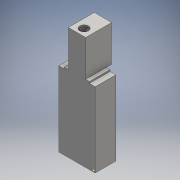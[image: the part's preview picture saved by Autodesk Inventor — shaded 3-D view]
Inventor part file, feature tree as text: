
AUTODESK INVENTOR PART (.ipt)
format: ipt  version: 2016 SP1 (Build 200210100, 210)  size: 351,744 bytes
history: native  units: mm
features: sketch x20, extrude x18, other x1
ambient origin geometry x8: Origin, YZ Plane, XZ Plane, XY Plane, X Axis, Y Axis, Z Axis, Center Point
bodies: Body1 (feature_tree)
feature tree (39):
  other  "Bryła1"
  extrude  "Wyciągnięcie proste1"  Depth=30.6mm
  extrude  "Wyciągnięcie proste2"  Depth=65.6mm
  extrude  "Wyciągnięcie proste3"  Depth=1.5mm TaperAngle=0.0deg
  extrude  "Wyciągnięcie proste4"  Depth=3.5mm
  sketch  "Szkic5"
  extrude  "Wyciągnięcie proste5"  Depth=3.5mm
  extrude  "Wyciągnięcie proste6"  Depth=3.5mm
  extrude  "Wyciągnięcie proste7"  Depth=3.5mm
  extrude  "Wyciągnięcie proste8"  Depth=3.5mm
  extrude  "Wyciągnięcie proste9"  Depth=3.5mm
  extrude  "Wyciągnięcie proste10"  Depth=3.5mm
  extrude  "Wyciągnięcie proste11"  Depth=3.5mm
  extrude  "Wyciągnięcie proste12"  Depth=6.8mm
  extrude  "Wyciągnięcie proste13"  Depth=6.8mm
  extrude  "Wyciągnięcie proste14"  Depth=6.8mm
  extrude  "Wyciągnięcie proste15"  Depth=6.8mm
  sketch  "Szkic17"
  extrude  "Wyciągnięcie proste16"  Depth=1.5mm TaperAngle=0.0deg
  extrude  "Wyciągnięcie proste17"  Depth=2.5mm
  extrude  "Wyciągnięcie proste18"  Depth=2.0mm
  sketch  "Szkic1"
  sketch  "Szkic2"
  sketch  "Szkic3"
  sketch  "Szkic4"
  sketch  "Szkic6"
  sketch  "Szkic7"
  sketch  "Szkic8"
  sketch  "Szkic9"
  sketch  "Szkic10"
  sketch  "Szkic11"
  sketch  "Szkic12"
  sketch  "Szkic13"
  sketch  "Szkic14"
  sketch  "Szkic15"
  sketch  "Szkic16"
  sketch  "Szkic18"
  sketch  "Szkic19"
  sketch  "Szkic20"
